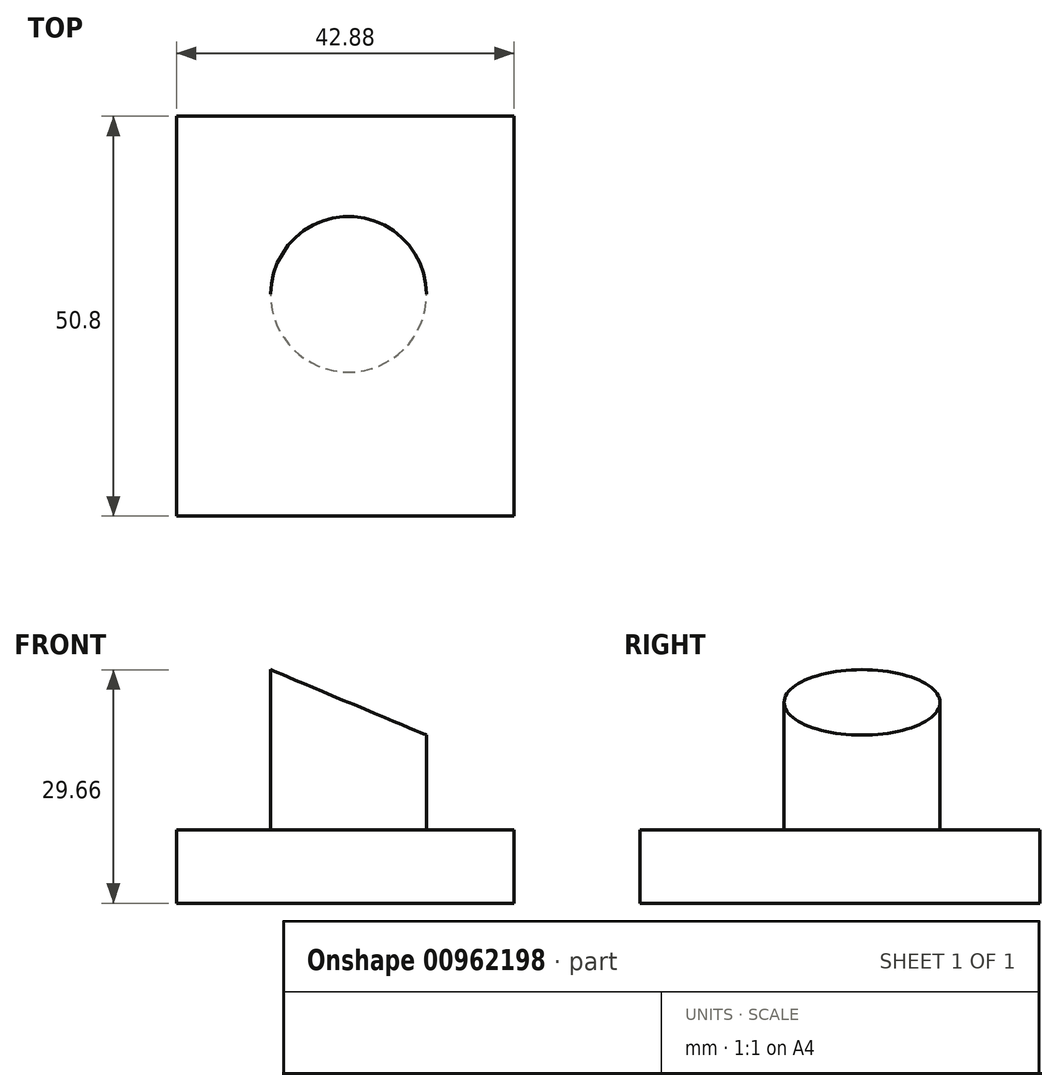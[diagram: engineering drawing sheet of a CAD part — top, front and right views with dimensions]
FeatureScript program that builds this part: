
annotation { "Feature Type Name" : "Feature", "Feature Type Description" : "" }
export const myFeature = defineFeature(function(context is Context, id is Id, definition is map)
    precondition{}
    {
        {
            var Q0;
            Q0=qCreatedBy(makeId("Front.planeOp"),FACE);
            var sketch = newSketch(context, id + "F0", { "sketchPlane" : qUnion([Q0])});
            skLineSegment(sketch, "E0", {"start": v(0, 0) * mm, "end": v(42.88, -17.99) * mm});
            skLineSegment(sketch, "E1", {"start": v(42.88, -17.99) * mm, "end": v(42.88, -34.68) * mm});
            skLineSegment(sketch, "E2", {"start": v(42.88, -34.68) * mm, "end": v(0, -34.68) * mm});
            skLineSegment(sketch, "E3", {"start": v(0, -34.68) * mm, "end": v(0, 0) * mm});
            skSolve(sketch);
        }
        {
            var Q0;
            Q0=makeQuery(id+"F0.imprint","IMPRINT",FACE,{"disambiguationData":[TD([[makeQuery(id+"F0.imprint","IMPRINT",EDGE,{"derivedFrom":sQuery(id+"F0.wireOp",EDGE,"E0")}),-1.0]])]});
            extrude(context, id + "F1", {"entities" : qUnion([Q0]), "depth" : 50.8 * mm, "offsetDistance" : 25.4 * mm});
        }
        {
            var Q0;
            Q0=qCreatedBy(makeId("Top.planeOp"),FACE);
            var sketch = newSketch(context, id + "F2", { "sketchPlane" : qUnion([Q0])});
            skLineSegment(sketch, "E4.bottom", {"start": v(-8.92, 7.63) * mm, "end": v(52.1, 7.63) * mm});
            skLineSegment(sketch, "E4.top", {"start": v(-8.92, -57.13) * mm, "end": v(52.1, -57.13) * mm});
            skLineSegment(sketch, "E4.left", {"start": v(-8.92, 7.63) * mm, "end": v(-8.92, -57.13) * mm});
            skLineSegment(sketch, "E4.right", {"start": v(52.1, 7.63) * mm, "end": v(52.1, -57.13) * mm});
            skCircle(sketch, "E5", {"center": v(21.87, -22.6) * mm, "radius": 9.91 * mm});
            skSolve(sketch);
        }
        {
            var Q0;
            Q0=makeQuery(id+"F2.imprint","IMPRINT",FACE,{"disambiguationData":[TD([[makeQuery(id+"F2.imprint","IMPRINT",EDGE,{"derivedFrom":sQuery(id+"F2.wireOp",EDGE,"E4.bottom")}),-1.0]])]});
            extrude(context, id + "F3", {"entities" : qUnion([Q0]), "operationType" : NewBodyOperationType.REMOVE, "oppositeDirection" : true, "depth" : 25.4 * mm, "offsetDistance" : 25.4 * mm});
        }
    });
